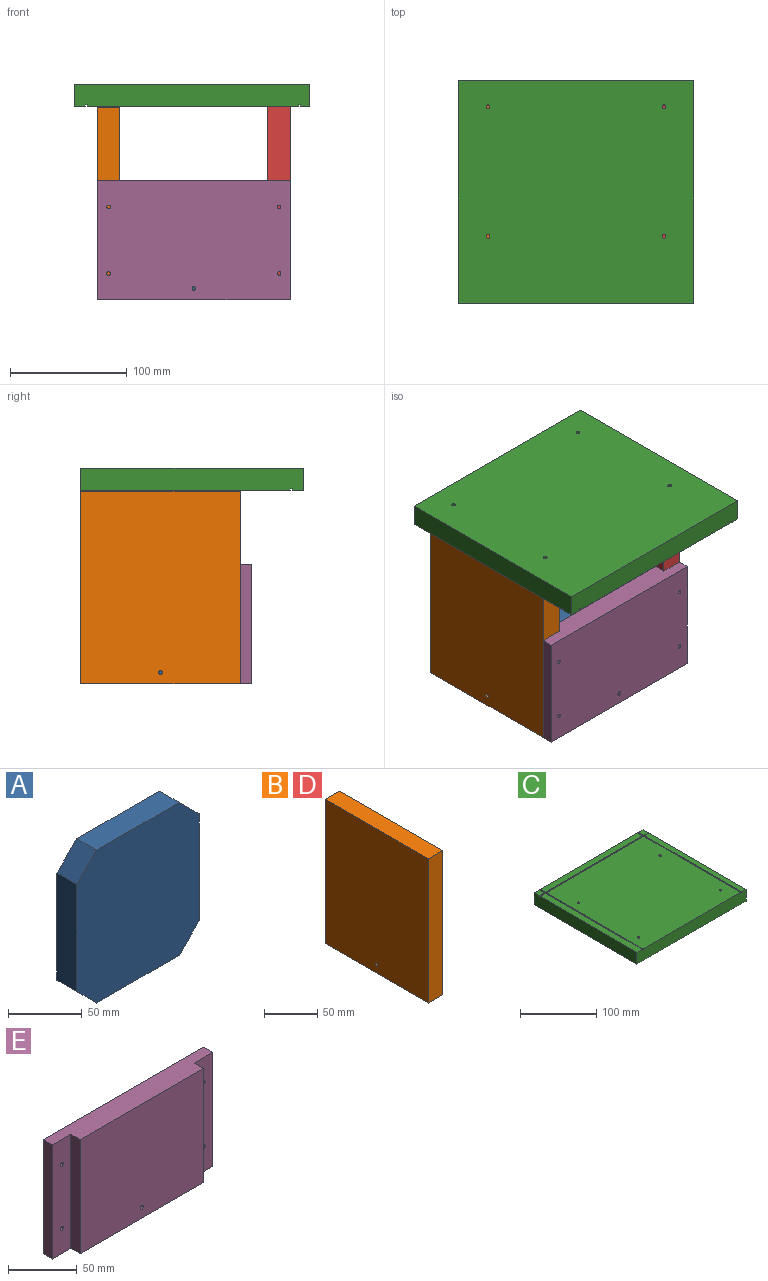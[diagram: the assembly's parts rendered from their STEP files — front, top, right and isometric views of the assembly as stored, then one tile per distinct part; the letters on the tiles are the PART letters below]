
ASSEMBLY  parts=5 mates=4
PART A: 10 faces, bbox 117.5x19.1x127 mm
  f0: plane 19.05x19.05mm, normal (0.71,0,0.71), area 513.2mm2, adj f1,f7,f8,f9
  f1: plane 79.38x19.05mm, normal (0,0,1), area 1512.1mm2, adj f0,f2,f8,f9
  f2: plane 19.05x19.05mm, normal (-0.71,0,0.71), area 513.2mm2, adj f1,f3,f8,f9
  f3: plane 88.9x19.05mm, normal (-1,0,0), area 1693.5mm2, adj f2,f4,f8,f9
  f4: plane 19.05x19.05mm, normal (-0.71,0,-0.71), area 513.2mm2, adj f3,f5,f8,f9
  f5: plane 79.38x19.05mm, normal (0,0,-1), area 1512.1mm2, adj f4,f6,f8,f9
  f6: plane 19.05x19.05mm, normal (0.71,0,-0.71), area 513.2mm2, adj f5,f7,f8,f9
  f7: plane 88.9x19.05mm, normal (1,0,0), area 1693.5mm2, adj f0,f6,f8,f9
  f8: plane 127x117.48mm, normal (0,-1,0), area 14193.5mm2, adj f0,f1,f2,f3,f4,f5,f6,f7
  f9: plane 127x117.48mm, normal (0,1,0), area 14193.5mm2, adj f0,f1,f2,f3,f4,f5,f6,f7
PART B: 7 faces, bbox 19.1x136.5x165.1 mm
  f0: plane 136.53x19.05mm, normal (0,0,-1), area 2600.8mm2, adj f1,f3,f4,f5
  f1: plane 165.1x19.05mm, normal (0,1,0), area 3145.2mm2, adj f0,f2,f4,f5
  f2: plane 136.53x19.05mm, normal (0,0,1), area 2600.8mm2, adj f1,f3,f4,f5
  f3: plane 165.1x19.05mm, normal (0,-1,0), area 3145.2mm2, adj f0,f2,f4,f5
  f4: plane 165.1x136.53mm, normal (1,0,0), area 22532.4mm2, adj f0,f1,f2,f3,f6
  f5: plane 165.1x136.53mm, normal (-1,0,0), area 22532.4mm2, adj f0,f1,f2,f3,f6
  f6: cylinder r=1.59mm len=19.05mm, axis (1,0,0), area 190mm2, adj f4,f5
PART C: 30 faces, bbox 201.6x190.5x19.1 mm
  f0: plane 190.5x19.05mm, normal (-1,0,0), area 3626.5mm2, adj f1,f4,f7,f9,f10,f17,f18,f25
  f1: plane 201.61x19.05mm, normal (0,1,0), area 3835.7mm2, adj f0,f2,f3,f8,f9,f10,f12,f13
  f2: plane 180.98x9.53mm, normal (0,0,1), area 1723.8mm2, adj f1,f13,f14,f15
  f3: plane 9.53x7.94mm, normal (0,0,1), area 75.6mm2, adj f1,f8,f11,f12
  f4: plane 179.39x9.53mm, normal (0,0,1), area 1708.7mm2, adj f0,f7,f18,f19
  f5: plane 180.98x179.39mm, normal (0,0,1), area 32433mm2, adj f7,f20,f21,f22,f26,f27,f28,f29
  f6: plane 179.39x7.94mm, normal (0,0,1), area 1423.9mm2, adj f7,f8,f23,f24
  f7: plane 201.61x19.05mm, normal (0,-1,0), area 3835.7mm2, adj f0,f4,f5,f6,f8,f10,f19,f20
  f8: plane 190.5x19.05mm, normal (1,0,0), area 3626.5mm2, adj f1,f3,f6,f7,f10,f11,f24,f25
  f9: plane 9.53x9.53mm, normal (0,0,1), area 90.7mm2, adj f0,f1,f16,f17
  f10: plane 201.61x190.5mm, normal (0,0,-1), area 38375.5mm2, adj f0,f1,f7,f8,f26,f27,f28,f29
  f11: plane 7.94x1.59mm, normal (0,-1,0), area 12.6mm2, adj f3,f8,f12,f25
  f12: plane 9.53x1.59mm, normal (-1,0,0), area 15.1mm2, adj f1,f3,f11,f25
  f13: plane 9.53x1.59mm, normal (1,0,0), area 15.1mm2, adj f1,f2,f14,f25
  f14: plane 180.98x1.59mm, normal (0,-1,0), area 287.3mm2, adj f2,f13,f15,f25
  f15: plane 9.53x1.59mm, normal (-1,0,0), area 15.1mm2, adj f1,f2,f14,f25
  f16: plane 9.53x1.59mm, normal (1,0,0), area 15.1mm2, adj f1,f9,f17,f25
  f17: plane 9.53x1.59mm, normal (0,-1,0), area 15.1mm2, adj f0,f9,f16,f25
  f18: plane 9.53x1.59mm, normal (0,1,0), area 15.1mm2, adj f0,f4,f19,f25
  f19: plane 179.39x1.59mm, normal (1,0,0), area 284.8mm2, adj f4,f7,f18,f25
  f20: plane 179.39x1.59mm, normal (-1,0,0), area 284.8mm2, adj f5,f7,f21,f25
  f21: plane 180.98x1.59mm, normal (0,1,0), area 287.3mm2, adj f5,f20,f22,f25
  f22: plane 179.39x1.59mm, normal (1,0,0), area 284.8mm2, adj f5,f7,f21,f25
  f23: plane 179.39x1.59mm, normal (-1,0,0), area 284.8mm2, adj f6,f7,f24,f25
  f24: plane 7.94x1.59mm, normal (0,1,0), area 12.6mm2, adj f6,f8,f23,f25
  f25: plane 201.61x190.5mm, normal (0,0,1), area 919.9mm2, adj f0,f1,f7,f8,f11,f12,f13,f14
  f26: cylinder r=1.59mm len=19.05mm, axis (0,0,1), area 190mm2, adj f5,f10
  f27: cylinder r=1.59mm len=19.05mm, axis (0,0,1), area 190mm2, adj f5,f10
  f28: cylinder r=1.59mm len=19.05mm, axis (0,0,1), area 190mm2, adj f5,f10
  f29: cylinder r=1.59mm len=19.05mm, axis (0,0,1), area 190mm2, adj f5,f10
PART D: same geometry as B
PART E: 15 faces, bbox 165.1x19.1x101.6 mm
  f0: plane 165.1x19.05mm, normal (0,0,-1), area 2782.3mm2, adj f1,f3,f4,f5,f6,f7,f8,f9
  f1: plane 101.6x9.53mm, normal (1,0,0), area 967.7mm2, adj f0,f2,f5,f7
  f2: plane 165.1x19.05mm, normal (0,0,1), area 2782.3mm2, adj f1,f3,f4,f5,f6,f7,f8,f9
  f3: plane 101.6x9.53mm, normal (-1,0,0), area 967.7mm2, adj f0,f2,f5,f9
  f4: plane 127x101.6mm, normal (0,-1,0), area 12895.3mm2, adj f0,f2,f6,f8,f13
  f5: plane 165.1x101.6mm, normal (0,1,0), area 16734.6mm2, adj f0,f1,f2,f3,f10,f11,f12,f13
  f6: plane 101.6x9.53mm, normal (1,0,0), area 967.7mm2, adj f0,f2,f4,f7
  f7: plane 101.6x19.05mm, normal (0,-1,0), area 1919.6mm2, adj f0,f1,f2,f6,f11,f12
  f8: plane 101.6x9.53mm, normal (-1,0,0), area 967.7mm2, adj f0,f2,f4,f9
  f9: plane 101.6x19.05mm, normal (0,-1,0), area 1919.6mm2, adj f0,f2,f3,f8,f10,f14
  f10: cylinder r=1.59mm len=9.53mm, axis (0,1,0), area 95mm2, adj f5,f9
  f11: cylinder r=1.59mm len=9.53mm, axis (0,1,0), area 95mm2, adj f5,f7
  f12: cylinder r=1.59mm len=9.53mm, axis (0,1,0), area 95mm2, adj f5,f7
  f13: cylinder r=1.59mm len=19.05mm, axis (0,1,0), area 190mm2, adj f4,f5
  f14: cylinder r=1.59mm len=9.53mm, axis (0,1,0), area 95mm2, adj f5,f9
PLACE A rot(axis=(-0.58,-0.58,0.58),120deg) t=(328.45,136.63,-274.46)mm
PLACE B t=(246.11,136.63,-192.21)mm
PLACE C rot(axis=(-1,0,0),180deg) t=(226.12,202.59,-90.07)mm
PLACE D t=(391.86,136.63,-191.67)mm
PLACE E rot(axis=(0,0,-1),180deg) t=(328.53,58.85,-223.75)mm
MATE planar A.f3 <-> E.f4  axis (0,-1,0) through (328.45,77.9,-264.94)mm
MATE planar D.f3 <-> E.f9  axis (0,-1,0) through (401.38,68.37,-191.67)mm
MATE planar C.f5 <-> D.f2  axis (0,0,-1) through (327.72,115.14,-109.12)mm
MATE planar B.f3 <-> E.f7  axis (0,-1,0) through (255.63,68.37,-192.21)mm
